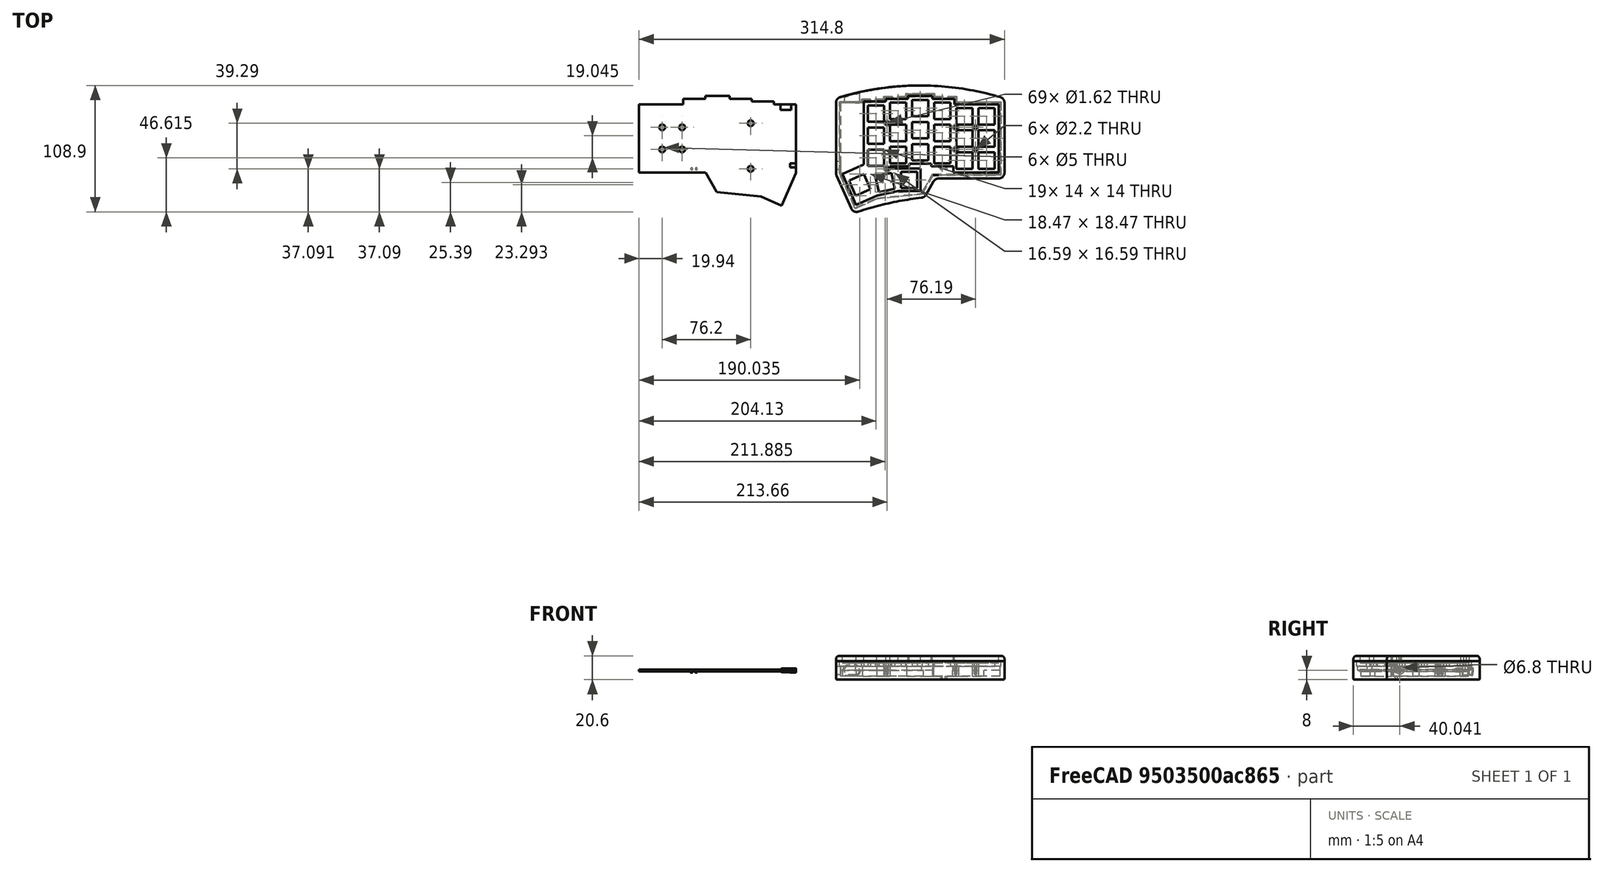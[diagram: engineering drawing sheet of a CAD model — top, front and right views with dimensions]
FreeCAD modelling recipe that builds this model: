
FCSTD DOCUMENT  (FreeCAD 0.21R33771 (Git))
Label: tiltedCaseSplitV1
License: All rights reserved
LicenseURL: http://en.wikipedia.org/wiki/All_rights_reserved
objects: Sketcher::SketchObject×10, PartDesign::Pad×10, PartDesign::SubShapeBinder×9, PartDesign::Pocket×8, PartDesign::Fillet×5, PartDesign::Body×3, Part::Mirroring×2, Mesh::Feature×2, PartDesign::ShapeBinder×1, PartDesign::Hole×1
note: 73 computed .brp shape members not serialized (recipe doc carries the construction recipe); baked Part::Feature solids carry a one-line shape summary decoded from their .brp

FEATURE [Sketcher::SketchObject] Sketch024  label="BodySketch"
  FullyConstrained = true
  MapMode = 5
  Support = -> [XY_Plane004]
  sketch-geometry (18):
    g0: LineSegment StartX=-154.9 StartY=-37.98 StartZ=0 EndX=-116.82 EndY=-37.98 EndZ=0
    g1: LineSegment StartX=-116.82 StartY=-37.98 StartZ=0 EndX=-116.82 EndY=-33.217 EndZ=0
    g2: LineSegment StartX=-116.82 StartY=-33.217 StartZ=0 EndX=-97.77 EndY=-33.217 EndZ=0
    g3: LineSegment StartX=-97.77 StartY=-33.217 StartZ=0 EndX=-97.77 EndY=-30.836 EndZ=0
    g4: LineSegment StartX=-97.77 StartY=-30.836 StartZ=0 EndX=-76.92 EndY=-30.836 EndZ=0
    g5: LineSegment StartX=-76.92 StartY=-30.836 StartZ=0 EndX=-76.92 EndY=-33.217 EndZ=0
    g6: LineSegment StartX=-76.92 StartY=-33.217 StartZ=0 EndX=-57.87 EndY=-33.217 EndZ=0
    g7: LineSegment StartX=-57.87 StartY=-33.217 StartZ=0 EndX=-57.87 EndY=-35.598 EndZ=0
    g8: LineSegment StartX=-57.87 StartY=-35.598 StartZ=0 EndX=-38.82 EndY=-35.598 EndZ=0
    g9: LineSegment StartX=-38.82 StartY=-35.598 StartZ=0 EndX=-38.82 EndY=-37.979 EndZ=0
    g10: LineSegment StartX=-38.82 StartY=-37.979 StartZ=0 EndX=-19.75 EndY=-37.979 EndZ=0
    g11: LineSegment StartX=-19.75 StartY=-37.979 StartZ=0 EndX=-19.75 EndY=-97.199 EndZ=0
    g12: LineSegment StartX=-19.75 StartY=-97.199 StartZ=0 EndX=-32.2083 EndY=-125.339 EndZ=0
    g13: LineSegment StartX=-32.2083 StartY=-125.339 StartZ=0 EndX=-49.87 EndY=-117.52 EndZ=0
    g14: LineSegment StartX=-49.87 StartY=-117.52 StartZ=0 EndX=-87.8774 EndY=-113.545 EndZ=0
    g15: LineSegment StartX=-87.8774 StartY=-113.545 StartZ=0 EndX=-97.37 EndY=-96.93 EndZ=0
    g16: LineSegment StartX=-97.37 StartY=-96.93 StartZ=0 EndX=-154.9 EndY=-96.93 EndZ=0
    g17: LineSegment StartX=-154.9 StartY=-96.93 StartZ=0 EndX=-154.9 EndY=-37.98 EndZ=0
  constraints (54):
    c: Horizontal(g0)
    c: Coincident(g0,g1)
    c: Vertical(g1)
    c: Coincident(g1,g2)
    c: Horizontal(g2)
    c: Coincident(g2,g3)
    c: Vertical(g3)
    c: Coincident(g3,g4)
    c: Horizontal(g4)
    c: Coincident(g4,g5)
    c: Vertical(g5)
    c: Coincident(g5,g6)
    c: Horizontal(g6)
    c: Coincident(g6,g7)
    c: Vertical(g7)
    c: Coincident(g7,g8)
    c: Horizontal(g8)
    c: Coincident(g8,g9)
    c: Vertical(g9)
    c: Coincident(g9,g10)
    c: Horizontal(g10)
    c: Coincident(g10,g11)
    c: Vertical(g11)
    c: Coincident(g11,g12)
    c: Coincident(g12,g13)
    c: Coincident(g13,g14)
    c: Coincident(g14,g15)
    c: Coincident(g15,g16)
    c: Horizontal(g16)
    c: Coincident(g16,g17)
    c: Coincident(g17,g0)
    c: Vertical(g17)
    c: DistanceX(g0,g-1) = 154.9
    c: DistanceY(g0,g-1) = 37.98
    c: DistanceX(g0,g0) = 38.08
    c: DistanceY(g1,g1) = 4.763
    c: DistanceY(g3,g3) = 2.381
    c: DistanceY(g5,g5) = 2.381
    c: DistanceY(g7,g7) = 2.381
    c: DistanceY(g9,g9) = 2.381
    c: DistanceX(g2,g2) = 19.05
    c: DistanceX(g4,g4) = 20.85
    c: DistanceX(g6,g6) = 19.05
    c: DistanceX(g8,g8) = 19.05
    c: DistanceX(g10,g10) = 19.07
    c: DistanceY(g17,g17) = 58.95
    c: DistanceX(g16,g16) = 57.53
    c: DistanceX(g15,g13) = 47.5
    c: DistanceY(g13,g15) = 20.59
    c: DistanceY(g11,g11) = 59.22
    c: Angle(g11,g12) = 2.72481
    c: Angle(g12,g13) = 1.5708
    c: Angle(g14,g13) = 2.829
    c: Angle(g14,g15) = 2.19405
FEATURE [PartDesign::Pad] Pad010  label="BodyPad"
  Direction = (0,0,1)
  Length = 1.6
  Length2 = 10
  Profile = -> Sketch024
  ReferenceAxis = -> Sketch024 [N_Axis]
  Type = 0
FEATURE [Sketcher::SketchObject] Sketch025  label="SkrewSketch"
  ExternalGeometry = -> [Pad010]
  FullyConstrained = true
  MapMode = 5
  Support = -> [XY_Plane004]
  sketch-geometry (6):
    g0: Circle CenterX=-134.96 CenterY=-57.929 CenterZ=0 NormalX=0 NormalY=0 NormalZ=1 AngleXU=0 Radius=2.5
    g1: Circle CenterX=-117.815 CenterY=-57.929 CenterZ=0 NormalX=0 NormalY=0 NormalZ=1 AngleXU=0 Radius=2.5
    g2: Circle CenterX=-58.76 CenterY=-54.359 CenterZ=0 NormalX=0 NormalY=0 NormalZ=1 AngleXU=0 Radius=2.5
    g3: Circle CenterX=-58.76 CenterY=-93.649 CenterZ=0 NormalX=0 NormalY=0 NormalZ=1 AngleXU=0 Radius=2.5
    g4: Circle CenterX=-117.815 CenterY=-76.979 CenterZ=0 NormalX=0 NormalY=0 NormalZ=1 AngleXU=0 Radius=2.5
    g5: Circle CenterX=-134.96 CenterY=-76.979 CenterZ=0 NormalX=0 NormalY=0 NormalZ=1 AngleXU=0 Radius=2.5
  constraints (18):
    c: Equal(g5,g0)
    c: Equal(g5,g1)
    c: Equal(g5,g4)
    c: Equal(g5,g2)
    c: Equal(g5,g3)
    c: Diameter(g5) = 5
    c: Horizontal(g0,g1)
    c: Horizontal(g5,g4)
    c: Vertical(g0,g5)
    c: Vertical(g1,g4)
    c: Vertical(g2,g3)
    c: DistanceY(g2,g-3) = 16.38
    c: DistanceX(g2,g-3) = 39.01
    c: DistanceX(g0,g1) = 17.145
    c: DistanceY(g5,g0) = 19.05
    c: DistanceY(g3,g2) = 39.29
    c: DistanceY(g3,g4) = 16.67
    c: DistanceX(g0,g2) = 76.2
FEATURE [PartDesign::Pocket] Pocket028  label="ScrewPocket"
  BaseFeature = -> Pad010
  Direction = (0,0,-1)
  Length = 2
  Length2 = 5
  Profile = -> Sketch025
  ReferenceAxis = -> Sketch025 [N_Axis]
  Reversed = true
  Type = 0
FEATURE [PartDesign::SubShapeBinder] Binder006  label="PcbPlateBinder"
  BindCopyOnChange = 0
  BindMode = 0
  ClaimChildren = false
  Context = -> Body005 [Binder006.]
  Fuse = false
  MakeFace = true
  Offset = 1.9
  OffsetFill = false
  OffsetIntersection = false
  OffsetJoinType = 1
  OffsetOpenResult = false
  PartialLoad = false
  Placement = pos=(0,0,4.6) rot=(0,0,1;0rad)
  Relative = true
  Support = -> [Body004[Pad010.Sketch024.]]
  _Version = 2
FEATURE [PartDesign::Pad] Pad011  label="PlateBodyPad"
  Direction = (0,0,1)
  Length = 8.9
  Length2 = 10
  Placement = pos=(0,0,4.6) rot=(0,0,1;0rad)
  Profile = -> Binder006
  Type = 0
FEATURE [Sketcher::SketchObject] Sketch026  label="PlateSwitchSketch"
  FullyConstrained = true
  MapMode = 5
  Support = -> [XY_Plane005]
  expr: Constraints[126] = .Constraints.switchDistance
  expr: Constraints[127] = .Constraints.switchDistance
  expr: Constraints[128] = .Constraints.switchDistance
  sketch-geometry (112):
    g0: Circle CenterX=-134.95 CenterY=-57.93 CenterZ=0 NormalX=0 NormalY=0 NormalZ=1 AngleXU=0 Radius=1.1
    g1: Circle CenterX=-134.95 CenterY=-76.98 CenterZ=0 NormalX=0 NormalY=0 NormalZ=1 AngleXU=0 Radius=1.1
    g2: Circle CenterX=-58.76 CenterY=-54.36 CenterZ=0 NormalX=0 NormalY=0 NormalZ=1 AngleXU=0 Radius=1.1
    g3: Circle CenterX=-58.76 CenterY=-93.65 CenterZ=0 NormalX=0 NormalY=0 NormalZ=1 AngleXU=0 Radius=1.1
    g4: LineSegment StartX=-151.48 StartY=-41.41 StartZ=0 EndX=-151.48 EndY=-55.41 EndZ=0
    g5: LineSegment StartX=-151.48 StartY=-55.41 StartZ=0 EndX=-137.48 EndY=-55.41 EndZ=0
    g6: LineSegment StartX=-137.48 StartY=-55.41 StartZ=0 EndX=-137.48 EndY=-41.41 EndZ=0
    g7: LineSegment StartX=-137.48 StartY=-41.41 StartZ=0 EndX=-151.48 EndY=-41.41 EndZ=0
    g8: GeomPoint X=-144.48 Y=-48.41 Z=0
    g9: LineSegment StartX=-151.48 StartY=-60.46 StartZ=0 EndX=-151.48 EndY=-74.46 EndZ=0
    g10: LineSegment StartX=-151.48 StartY=-74.46 StartZ=0 EndX=-137.48 EndY=-74.46 EndZ=0
    g11: LineSegment StartX=-137.48 StartY=-74.46 StartZ=0 EndX=-137.48 EndY=-60.46 EndZ=0
    g12: LineSegment StartX=-137.48 StartY=-60.46 StartZ=0 EndX=-151.48 EndY=-60.46 EndZ=0
    g13: GeomPoint X=-144.48 Y=-67.46 Z=0
    g14: LineSegment StartX=-151.48 StartY=-79.51 StartZ=0 EndX=-151.48 EndY=-93.51 EndZ=0
    g15: LineSegment StartX=-151.48 StartY=-93.51 StartZ=0 EndX=-137.48 EndY=-93.51 EndZ=0
    g16: LineSegment StartX=-137.48 StartY=-93.51 StartZ=0 EndX=-137.48 EndY=-79.51 EndZ=0
    g17: LineSegment StartX=-137.48 StartY=-79.51 StartZ=0 EndX=-151.48 EndY=-79.51 EndZ=0
    g18: GeomPoint X=-144.48 Y=-86.51 Z=0
    g19: LineSegment StartX=-132.43 StartY=-41.41 StartZ=0 EndX=-132.43 EndY=-55.41 EndZ=0
    g20: LineSegment StartX=-132.43 StartY=-55.41 StartZ=0 EndX=-118.43 EndY=-55.41 EndZ=0
    g21: LineSegment StartX=-118.43 StartY=-55.41 StartZ=0 EndX=-118.43 EndY=-41.41 EndZ=0
    g22: LineSegment StartX=-118.43 StartY=-41.41 StartZ=0 EndX=-132.43 EndY=-41.41 EndZ=0
    g23: GeomPoint X=-125.43 Y=-48.41 Z=0
    g24: LineSegment StartX=-132.43 StartY=-60.46 StartZ=0 EndX=-132.43 EndY=-74.46 EndZ=0
    g25: LineSegment StartX=-132.43 StartY=-74.46 StartZ=0 EndX=-118.43 EndY=-74.46 EndZ=0
    g26: LineSegment StartX=-118.43 StartY=-74.46 StartZ=0 EndX=-118.43 EndY=-60.46 EndZ=0
    g27: LineSegment StartX=-118.43 StartY=-60.46 StartZ=0 EndX=-132.43 EndY=-60.46 EndZ=0
    g28: GeomPoint X=-125.43 Y=-67.46 Z=0
    g29: LineSegment StartX=-132.43 StartY=-79.51 StartZ=0 EndX=-132.43 EndY=-93.51 EndZ=0
    g30: LineSegment StartX=-132.43 StartY=-93.51 StartZ=0 EndX=-118.43 EndY=-93.51 EndZ=0
    g31: LineSegment StartX=-118.43 StartY=-93.51 StartZ=0 EndX=-118.43 EndY=-79.51 EndZ=0
    g32: LineSegment StartX=-118.43 StartY=-79.51 StartZ=0 EndX=-132.43 EndY=-79.51 EndZ=0
    g33: GeomPoint X=-125.43 Y=-86.51 Z=0
    g34: LineSegment StartX=-113.38 StartY=-36.65 StartZ=0 EndX=-113.38 EndY=-50.65 EndZ=0
    g35: LineSegment StartX=-113.38 StartY=-50.65 StartZ=0 EndX=-99.38 EndY=-50.65 EndZ=0
    g36: LineSegment StartX=-99.38 StartY=-50.65 StartZ=0 EndX=-99.38 EndY=-36.65 EndZ=0
    g37: LineSegment StartX=-99.38 StartY=-36.65 StartZ=0 EndX=-113.38 EndY=-36.65 EndZ=0
    g38: GeomPoint X=-106.38 Y=-43.65 Z=0
    g39: LineSegment StartX=-94.33 StartY=-34.27 StartZ=0 EndX=-94.33 EndY=-48.27 EndZ=0
    g40: LineSegment StartX=-94.33 StartY=-48.27 StartZ=0 EndX=-80.33 EndY=-48.27 EndZ=0
    g41: LineSegment StartX=-80.33 StartY=-48.27 StartZ=0 EndX=-80.33 EndY=-34.27 EndZ=0
    g42: LineSegment StartX=-80.33 StartY=-34.27 StartZ=0 EndX=-94.33 EndY=-34.27 EndZ=0
    g43: GeomPoint X=-87.33 Y=-41.27 Z=0
    g44: LineSegment StartX=-75.28 StartY=-36.65 StartZ=0 EndX=-75.28 EndY=-50.65 EndZ=0
    g45: LineSegment StartX=-75.28 StartY=-50.65 StartZ=0 EndX=-61.28 EndY=-50.65 EndZ=0
    g46: LineSegment StartX=-61.28 StartY=-50.65 StartZ=0 EndX=-61.28 EndY=-36.65 EndZ=0
    g47: LineSegment StartX=-61.28 StartY=-36.65 StartZ=0 EndX=-75.28 EndY=-36.65 EndZ=0
    g48: GeomPoint X=-68.28 Y=-43.65 Z=0
    g49: LineSegment StartX=-56.23 StartY=-39.03 StartZ=0 EndX=-56.23 EndY=-53.03 EndZ=0
    g50: LineSegment StartX=-56.23 StartY=-53.03 StartZ=0 EndX=-42.23 EndY=-53.03 EndZ=0
    g51: LineSegment StartX=-42.23 StartY=-53.03 StartZ=0 EndX=-42.23 EndY=-39.03 EndZ=0
    g52: LineSegment StartX=-42.23 StartY=-39.03 StartZ=0 EndX=-56.23 EndY=-39.03 EndZ=0
    g53: GeomPoint X=-49.23 Y=-46.03 Z=0
    g54: LineSegment StartX=-113.38 StartY=-55.7 StartZ=0 EndX=-113.38 EndY=-69.7 EndZ=0
    g55: LineSegment StartX=-113.38 StartY=-69.7 StartZ=0 EndX=-99.38 EndY=-69.7 EndZ=0
    g56: LineSegment StartX=-99.38 StartY=-69.7 StartZ=0 EndX=-99.38 EndY=-55.7 EndZ=0
    g57: LineSegment StartX=-99.38 StartY=-55.7 StartZ=0 EndX=-113.38 EndY=-55.7 EndZ=0
    g58: GeomPoint X=-106.38 Y=-62.7 Z=0
    g59: LineSegment StartX=-113.38 StartY=-74.745 StartZ=0 EndX=-113.38 EndY=-88.745 EndZ=0
    g60: LineSegment StartX=-113.38 StartY=-88.745 StartZ=0 EndX=-99.38 EndY=-88.745 EndZ=0
    g61: LineSegment StartX=-99.38 StartY=-88.745 StartZ=0 EndX=-99.38 EndY=-74.745 EndZ=0
    g62: LineSegment StartX=-99.38 StartY=-74.745 StartZ=0 EndX=-113.38 EndY=-74.745 EndZ=0
    g63: GeomPoint X=-106.38 Y=-81.745 Z=0
    g64: LineSegment StartX=-94.33 StartY=-53.32 StartZ=0 EndX=-94.33 EndY=-67.32 EndZ=0
    g65: LineSegment StartX=-94.33 StartY=-67.32 StartZ=0 EndX=-80.33 EndY=-67.32 EndZ=0
    g66: LineSegment StartX=-80.33 StartY=-67.32 StartZ=0 EndX=-80.33 EndY=-53.32 EndZ=0
    g67: LineSegment StartX=-80.33 StartY=-53.32 StartZ=0 EndX=-94.33 EndY=-53.32 EndZ=0
    g68: GeomPoint X=-87.33 Y=-60.32 Z=0
    g69: LineSegment StartX=-94.33 StartY=-72.365 StartZ=0 EndX=-94.33 EndY=-86.365 EndZ=0
    g70: LineSegment StartX=-94.33 StartY=-86.365 StartZ=0 EndX=-80.33 EndY=-86.365 EndZ=0
    g71: LineSegment StartX=-80.33 StartY=-86.365 StartZ=0 EndX=-80.33 EndY=-72.365 EndZ=0
    g72: LineSegment StartX=-80.33 StartY=-72.365 StartZ=0 EndX=-94.33 EndY=-72.365 EndZ=0
    g73: GeomPoint X=-87.33 Y=-79.365 Z=0
    g74: LineSegment StartX=-75.28 StartY=-55.7 StartZ=0 EndX=-75.28 EndY=-69.7 EndZ=0
    g75: LineSegment StartX=-75.28 StartY=-69.7 StartZ=0 EndX=-61.28 EndY=-69.7 EndZ=0
    g76: LineSegment StartX=-61.28 StartY=-69.7 StartZ=0 EndX=-61.28 EndY=-55.7 EndZ=0
    g77: LineSegment StartX=-61.28 StartY=-55.7 StartZ=0 EndX=-75.28 EndY=-55.7 EndZ=0
    g78: GeomPoint X=-68.28 Y=-62.7 Z=0
    g79: LineSegment StartX=-75.28 StartY=-74.75 StartZ=0 EndX=-75.28 EndY=-88.75 EndZ=0
    g80: LineSegment StartX=-75.28 StartY=-88.75 StartZ=0 EndX=-61.28 EndY=-88.75 EndZ=0
    g81: LineSegment StartX=-61.28 StartY=-88.75 StartZ=0 EndX=-61.28 EndY=-74.75 EndZ=0
    g82: LineSegment StartX=-61.28 StartY=-74.75 StartZ=0 EndX=-75.28 EndY=-74.75 EndZ=0
    g83: GeomPoint X=-68.28 Y=-81.75 Z=0
    g84: LineSegment StartX=-56.23 StartY=-58.08 StartZ=0 EndX=-56.23 EndY=-72.08 EndZ=0
    g85: LineSegment StartX=-56.23 StartY=-72.08 StartZ=0 EndX=-42.23 EndY=-72.08 EndZ=0
    g86: LineSegment StartX=-42.23 StartY=-72.08 StartZ=0 EndX=-42.23 EndY=-58.08 EndZ=0
    g87: LineSegment StartX=-42.23 StartY=-58.08 StartZ=0 EndX=-56.23 EndY=-58.08 EndZ=0
    g88: GeomPoint X=-49.23 Y=-65.08 Z=0
    g89: LineSegment StartX=-56.23 StartY=-77.125 StartZ=0 EndX=-56.23 EndY=-91.125 EndZ=0
    g90: LineSegment StartX=-56.23 StartY=-91.125 StartZ=0 EndX=-42.23 EndY=-91.125 EndZ=0
    g91: LineSegment StartX=-42.23 StartY=-91.125 StartZ=0 EndX=-42.23 EndY=-77.125 EndZ=0
    g92: LineSegment StartX=-42.23 StartY=-77.125 StartZ=0 EndX=-56.23 EndY=-77.125 EndZ=0
    g93: GeomPoint X=-49.23 Y=-84.125 Z=0
    g94: LineSegment StartX=-84.805 StartY=-96.17 StartZ=0 EndX=-84.805 EndY=-110.17 EndZ=0
    g95: LineSegment StartX=-84.805 StartY=-110.17 StartZ=0 EndX=-70.805 EndY=-110.17 EndZ=0
    g96: LineSegment StartX=-70.805 StartY=-110.17 StartZ=0 EndX=-70.805 EndY=-96.17 EndZ=0
    g97: LineSegment StartX=-70.805 StartY=-96.17 StartZ=0 EndX=-84.805 EndY=-96.17 EndZ=0
    g98: GeomPoint X=-77.805 Y=-103.17 Z=0
    g99: LineSegment StartX=-62.3853 StartY=-97.0536 StartZ=0 EndX=-65.2818 EndY=-110.751 EndZ=0
    g100: LineSegment StartX=-65.2818 StartY=-110.751 StartZ=0 EndX=-51.5847 EndY=-113.647 EndZ=0
    g101: LineSegment StartX=-51.5847 StartY=-113.647 StartZ=0 EndX=-48.6882 EndY=-99.95 EndZ=0
    g102: LineSegment StartX=-48.6882 StartY=-99.95 StartZ=0 EndX=-62.3853 EndY=-97.0536 EndZ=0
    g103: GeomPoint X=-56.985 Y=-105.35 Z=0
    g104: LineSegment StartX=-38.702 StartY=-98.2125 StartZ=0 EndX=-44.3695 EndY=-111.014 EndZ=0
    g105: LineSegment StartX=-44.3695 StartY=-111.014 StartZ=0 EndX=-31.568 EndY=-116.682 EndZ=0
    g106: LineSegment StartX=-31.568 StartY=-116.682 StartZ=0 EndX=-25.9005 EndY=-103.88 EndZ=0
    g107: LineSegment StartX=-25.9005 StartY=-103.88 StartZ=0 EndX=-38.702 EndY=-98.2125 EndZ=0
    g108: GeomPoint X=-35.135 Y=-107.447 Z=0
    g109: GeomPoint X=-77.805 Y=-87.5575 Z=0
    g110: Circle CenterX=-117.85 CenterY=-57.93 CenterZ=0 NormalX=0 NormalY=0 NormalZ=1 AngleXU=0 Radius=1.1
    g111: Circle CenterX=-117.85 CenterY=-76.98 CenterZ=0 NormalX=0 NormalY=0 NormalZ=1 AngleXU=0 Radius=1.1
  constraints (292):
    c: Equal(g0,g1)
    c: Equal(g0,g2)
    c: Equal(g0,g3)
    c: Diameter(g0) = 2.2
    c: Vertical(g1,g0)
    c: DistanceY(g1,g0) = 19.05
    c: Vertical(g2,g3)
    c: DistanceY(g3,g2) = 39.29
    c: Coincident(g4,g5)
    c: Coincident(g5,g6)
    c: Coincident(g6,g7)
    c: Coincident(g7,g4)
    c: Horizontal(g5)
    c: Horizontal(g7)
    c: Vertical(g4)
    c: Vertical(g6)
    c: Symmetric(g5,g4,g8)
    c: DistanceX(g7,g7) = 14
    c: Equal(g7,g6)
    c: Coincident(g9,g10)
    c: Coincident(g10,g11)
    c: Coincident(g11,g12)
    c: Coincident(g12,g9)
    c: Horizontal(g10)
    c: Horizontal(g12)
    c: Vertical(g9)
    c: Vertical(g11)
    c: Symmetric(g10,g9,g13)
    c: Equal(g11,g12)
    c: DistanceX(g12,g12) = 14
    c: Coincident(g14,g15)
    c: Coincident(g15,g16)
    c: Coincident(g16,g17)
    c: Coincident(g17,g14)
    c: Horizontal(g15)
    c: Horizontal(g17)
    c: Vertical(g14)
    c: Vertical(g16)
    c: Symmetric(g15,g14,g18)
    c: Equal(g17,g16)
    c: DistanceX(g17,g17) = 14
    c: Coincident(g19,g20)
    c: Coincident(g20,g21)
    c: Coincident(g21,g22)
    c: Coincident(g22,g19)
    c: Horizontal(g20)
    c: Horizontal(g22)
    c: Vertical(g19)
    c: Vertical(g21)
    c: Symmetric(g20,g19,g23)
    c: Equal(g22,g21)
    c: DistanceX(g22,g22) = 14
    c: Horizontal(g23,g8)
    c: DistanceX(g8,g23) = 19.05  'switchDistance'
    c: Vertical(g18,g13)
    c: Symmetric(g18,g8,g13)
    c: Coincident(g24,g25)
    c: Coincident(g25,g26)
    c: Coincident(g26,g27)
    c: Coincident(g27,g24)
    c: Horizontal(g25)
    c: Horizontal(g27)
    c: Vertical(g24)
    c: Vertical(g26)
    c: Symmetric(g25,g24,g28)
    c: Coincident(g29,g30)
    c: Coincident(g30,g31)
    c: Coincident(g31,g32)
    c: Coincident(g32,g29)
    c: Horizontal(g30)
    c: Horizontal(g32)
    c: Vertical(g29)
    c: Vertical(g31)
    c: Symmetric(g30,g29,g33)
    c: Horizontal(g33,g18)
    c: Vertical(g33,g28)
    c: Vertical(g28,g23)
    c: Equal(g27,g26)
    c: DistanceX(g27,g27) = 14
    c: Equal(g32,g31)
    c: DistanceX(g32,g32) = 14
    c: Horizontal(g28,g13)
    c: Coincident(g34,g35)
    c: Coincident(g35,g36)
    c: Coincident(g36,g37)
    c: Coincident(g37,g34)
    c: Horizontal(g35)
    c: Horizontal(g37)
    c: Vertical(g34)
    c: Vertical(g36)
    c: Symmetric(g35,g34,g38)
    c: Coincident(g39,g40)
    c: Coincident(g40,g41)
    c: Coincident(g41,g42)
    c: Coincident(g42,g39)
    c: Horizontal(g40)
    c: Horizontal(g42)
    c: Vertical(g39)
    c: Vertical(g41)
    c: Symmetric(g40,g39,g43)
    c: Coincident(g44,g45)
    c: Coincident(g45,g46)
    c: Coincident(g46,g47)
    c: Coincident(g47,g44)
    c: Horizontal(g45)
    c: Horizontal(g47)
    c: Vertical(g44)
    c: Vertical(g46)
    c: Symmetric(g45,g44,g48)
    c: Coincident(g49,g50)
    c: Coincident(g50,g51)
    c: Coincident(g51,g52)
    c: Coincident(g52,g49)
    c: Horizontal(g50)
    c: Horizontal(g52)
    c: Vertical(g49)
    c: Vertical(g51)
    c: Symmetric(g50,g49,g53)
    c: Equal(g37,g36)
    c: Equal(g42,g41)
    c: Equal(g47,g46)
    c: Equal(g52,g51)
    c: DistanceX(g37,g37) = 14
    c: DistanceX(g42,g42) = 14
    c: DistanceX(g47,g47) = 14
    c: DistanceX(g52,g52) = 14
    c: DistanceX(g23,g38) = 19.05
    c: DistanceX(g38,g43) = 19.05
    c: DistanceX(g43,g48) = 19.05
    c: DistanceX(g48,g53) = 19.05
    c: Coincident(g54,g55)
    c: Coincident(g55,g56)
    c: Coincident(g56,g57)
    c: Coincident(g57,g54)
    c: Horizontal(g55)
    c: Horizontal(g57)
    c: Vertical(g54)
    c: Vertical(g56)
    c: Symmetric(g55,g54,g58)
    c: Coincident(g59,g60)
    c: Coincident(g60,g61)
    c: Coincident(g61,g62)
    c: Coincident(g62,g59)
    c: Horizontal(g60)
    c: Horizontal(g62)
    c: Vertical(g59)
    c: Vertical(g61)
    c: Symmetric(g60,g59,g63)
    c: Equal(g57,g56)
    c: DistanceX(g57,g57) = 14
    c: Equal(g62,g61)
    c: DistanceX(g62,g62) = 14
    c: Vertical(g63,g58)
    c: Vertical(g58,g38)
    c: DistanceY(g11,g5) = 5.05  'switchDepthDistance'
    c: DistanceY(g56,g35) = 5.05
    c: DistanceY(g61,g55) = 5.045
    c: Coincident(g64,g65)
    c: Coincident(g65,g66)
    c: Coincident(g66,g67)
    c: Coincident(g67,g64)
    c: Horizontal(g65)
    c: Horizontal(g67)
    c: Vertical(g64)
    c: Vertical(g66)
    c: Symmetric(g65,g64,g68)
    c: Coincident(g69,g70)
    c: Coincident(g70,g71)
    c: Coincident(g71,g72)
    c: Coincident(g72,g69)
    c: Horizontal(g70)
    c: Horizontal(g72)
    c: Vertical(g69)
    c: Vertical(g71)
    c: Symmetric(g70,g69,g73)
    c: Vertical(g73,g68)
    c: Vertical(g68,g43)
    c: Equal(g67,g66)
    c: DistanceX(g67,g67) = 14
    c: Equal(g72,g71)
    c: DistanceX(g72,g72) = 14
    c: DistanceY(g66,g40) = 5.05
    c: DistanceY(g71,g65) = 5.045
    c: Coincident(g74,g75)
    c: Coincident(g75,g76)
    c: Coincident(g76,g77)
    c: Coincident(g77,g74)
    c: Horizontal(g75)
    c: Horizontal(g77)
    c: Vertical(g74)
    c: Vertical(g76)
    c: Symmetric(g75,g74,g78)
    c: Coincident(g79,g80)
    c: Coincident(g80,g81)
    c: Coincident(g81,g82)
    c: Coincident(g82,g79)
    c: Horizontal(g80)
    c: Horizontal(g82)
    c: Vertical(g79)
    c: Vertical(g81)
    c: Symmetric(g80,g79,g83)
    c: Coincident(g84,g85)
    c: Coincident(g85,g86)
    c: Coincident(g86,g87)
    c: Coincident(g87,g84)
    c: Horizontal(g85)
    c: Horizontal(g87)
    c: Vertical(g84)
    c: Vertical(g86)
    c: Symmetric(g85,g84,g88)
    c: Coincident(g89,g90)
    c: Coincident(g90,g91)
    c: Coincident(g91,g92)
    c: Coincident(g92,g89)
    c: Horizontal(g90)
    c: Horizontal(g92)
    c: Vertical(g89)
    c: Vertical(g91)
    c: Symmetric(g90,g89,g93)
    c: Vertical(g83,g78)
    c: Vertical(g78,g48)
    c: Equal(g77,g76)
    c: DistanceX(g77,g77) = 14
    c: Equal(g82,g81)
    c: DistanceX(g82,g82) = 14
    c: Equal(g87,g86)
    c: Equal(g91,g92)
    c: DistanceX(g87,g87) = 14
    c: DistanceX(g92,g92) = 14
    c: Vertical(g93,g88)
    c: Vertical(g88,g53) = 5.05
    c: DistanceY(g76,g45) = 5.05
    c: DistanceY(g81,g75) = 5.05
    c: DistanceY(g86,g50) = 5.05
    c: DistanceY(g91,g85) = 5.045
    c: Coincident(g94,g95)
    c: Coincident(g95,g96)
    c: Coincident(g96,g97)
    c: Coincident(g97,g94)
    c: Horizontal(g95)
    c: Horizontal(g97)
    c: Vertical(g94)
    c: Vertical(g96)
    c: Symmetric(g95,g94,g98)
    c: Coincident(g99,g100)
    c: Coincident(g100,g101)
    c: Coincident(g101,g102)
    c: Coincident(g102,g99)
    c: Symmetric(g100,g99,g103)
    c: Coincident(g104,g105)
    c: Coincident(g105,g106)
    c: Coincident(g106,g107)
    c: Coincident(g107,g104)
    c: Symmetric(g105,g104,g108)
    c: Equal(g97,g96)
    c: DistanceX(g97,g97) = 14
    c: Symmetric(g70,g79,g109)
    c: Vertical(g109,g98)
    c: Equal(g102,g101)
    c: Equal(g101,g100)
    c: Equal(g100,g99)
    c: Equal(g107,g106)
    c: Equal(g106,g105)
    c: Equal(g105,g104)
    c: Angle(g102,g101) = 1.5708
    c: Angle(g107,g106) = 1.5708
    c: Angle(g99,g96) = 0.208392
    c: Distance(g104,g106) = 14
    c: Distance(g99,g101) = 14
    c: DistanceX(g4,g-1) = 151.48
    c: DistanceY(g4,g-1) = 41.41
    c: DistanceY(g49,g-1) = 39.03
    c: DistanceY(g46,g-1) = 36.65
    c: DistanceY(g41,g-1) = 34.27
    c: DistanceY(g36,g-1) = 36.65
    c: DistanceY(g96,g-1) = 96.17
    c: DistanceY(g101,g-1) = 99.95
    c: DistanceY(g106,g-1) = 103.88
    c: DistanceX(g103,g108) = 21.85
    c: DistanceX(g98,g103) = 20.82
    c: Angle(g104,g101) = 0.208392
    c: DistanceY(g9,g4) = 5.05
    c: DistanceX(g2,g-1) = 58.76
    c: DistanceX(g0,g-1) = 134.95
    c: DistanceY(g2,g-1) = 54.36
    c: DistanceY(g0,g-1) = 57.93
    c: Vertical(g111,g110)
    c: Equal(g0,g110)
    c: Equal(g110,g111)
    c: Horizontal(g110,g0)
    c: Horizontal(g111,g1)
    c: DistanceX(g0,g110) = 17.1
FEATURE [PartDesign::SubShapeBinder] Binder008  label="PcbOuterBinder"
  BindCopyOnChange = 0
  BindMode = 0
  ClaimChildren = false
  Context = -> Body006 [Binder008.]
  Fuse = false
  MakeFace = true
  Offset = 5
  OffsetFill = false
  OffsetIntersection = false
  OffsetJoinType = 1
  OffsetOpenResult = false
  PartialLoad = false
  Relative = true
  Support = -> [Body004[Pad010.Sketch024.]]
  _Version = 2
FEATURE [Sketcher::SketchObject] Sketch027  label="OuterBodySketch"
  AttachmentOffset = pos=(0,0,-7) rot=(0,0,1;0rad)
  ExternalGeometry = -> [Binder008]
  FullyConstrained = true
  MapMode = 5
  Placement = pos=(0,0,-7) rot=(0,0,1;0rad)
  Support = -> [XY_Plane006]
  sketch-geometry (9):
    g0: LineSegment StartX=-159.9 StartY=-32.98 StartZ=0 EndX=-159.9 EndY=-101.93 EndZ=0
    g1: LineSegment StartX=-159.9 StartY=-101.93 StartZ=0 EndX=-100.272 EndY=-101.93 EndZ=0
    g2: LineSegment StartX=-100.272 StartY=-101.93 StartZ=0 EndX=-90.9471 EndY=-118.252 EndZ=0
    g3: LineSegment StartX=-29.6604 StartY=-131.935 StartZ=0 EndX=-14.75 EndY=-98.2563 EndZ=0
    g4: LineSegment StartX=-14.75 StartY=-98.2563 StartZ=0 EndX=-14.75 EndY=-32.979 EndZ=0
    g5: ArcOfCircle CenterX=-120.398 CenterY=-394.245 CenterZ=0 NormalX=0 NormalY=0 NormalZ=1 AngleXU=0 Radius=277.56 StartAngle=1.23776 EndAngle=1.46449
    g6: ArcOfCircle CenterX=-87.3234 CenterY=-263.74 CenterZ=0 NormalX=0 NormalY=0 NormalZ=1 AngleXU=0 Radius=241.904 StartAngle=1.26609 EndAngle=1.87551
    g7: GeomPoint X=-87.345 Y=-25.836 Z=0
    g8: GeomPoint X=-87.345 Y=-21.836 Z=0
  constraints (19):
    c: Coincident(g0,g-3)
    c: Coincident(g0,g-4)
    c: Coincident(g0,g1)
    c: Coincident(g1,g-5)
    c: Coincident(g1,g2)
    c: Coincident(g2,g-6)
    c: Coincident(g3,g-7)
    c: Coincident(g3,g-8)
    c: Coincident(g3,g4)
    c: Coincident(g4,g-9)
    c: PointOnObject(g8,g6)
    c: Symmetric(g-10,g-10,g7)
    c: Vertical(g8,g7)
    c: DistanceY(g7,g8) = 4
    c: Coincident(g6,g4)
    c: Coincident(g6,g0)
    c: Coincident(g5,g3)
    c: Coincident(g5,g2)
    c: Radius(g5) = 277.56
FEATURE [PartDesign::Pad] Pad012  label="OuterBodyPad"
  Direction = (0,0,1)
  Length = 16
  Length2 = 10
  Profile = -> Sketch027
  ReferenceAxis = -> Sketch027 [N_Axis]
  Type = 0
FEATURE [PartDesign::SubShapeBinder] Binder009  label="PcbInnerBinder"
  BindCopyOnChange = 0
  BindMode = 0
  ClaimChildren = false
  Context = -> Body006 [Binder009.]
  Fuse = false
  MakeFace = true
  Offset = 1.2
  OffsetFill = false
  OffsetIntersection = false
  OffsetJoinType = 1
  OffsetOpenResult = false
  PartialLoad = false
  Placement = pos=(0,0,-4) rot=(0,0,1;0rad)
  Relative = true
  Support = -> [Body004[Pad010.Sketch024.]]
  _Version = 2
FEATURE [PartDesign::Pocket] Pocket031  label="InnerPocket"
  BaseFeature = -> Pad012
  Direction = (0,0,-1)
  Length = 8
  Length2 = 5
  Profile = -> Binder009
  Reversed = true
  Type = 1
FEATURE [PartDesign::SubShapeBinder] Binder010  label="PcbCliffBinder"
  BindCopyOnChange = 0
  BindMode = 0
  ClaimChildren = false
  Context = -> Body006 [Binder010.]
  Fuse = false
  MakeFace = true
  Offset = 2
  OffsetFill = false
  OffsetIntersection = false
  OffsetJoinType = 1
  OffsetOpenResult = false
  PartialLoad = false
  Placement = pos=(0,0,4.6) rot=(0,0,1;0rad)
  Relative = true
  Support = -> [Body004[Pad010.Sketch024.]]
  _Version = 2
FEATURE [PartDesign::Pocket] Pocket032  label="CliffPocket"
  BaseFeature = -> Pocket031
  Direction = (0,0,-1)
  Length = 3.4
  Length2 = 5
  Profile = -> Binder010
  Reversed = true
  Type = 1
FEATURE [PartDesign::ShapeBinder] ShapeBinder  label="PcbSkrewBinder"
  Support = -> [Sketch025]
  TraceSupport = false
FEATURE [Sketcher::SketchObject] Sketch  label="SkrewSupportSketch"
  ExternalGeometry = -> [ShapeBinder,Pocket032]
  FullyConstrained = true
  MapMode = 5
  Placement = pos=(0,0,-4) rot=(0,0,1;0rad)
  Support = -> [Pocket032]
  sketch-geometry (30):
    g0: Circle CenterX=-134.96 CenterY=-57.929 CenterZ=0 NormalX=0 NormalY=0 NormalZ=1 AngleXU=0 Radius=2.6
    g1: Circle CenterX=-134.96 CenterY=-76.979 CenterZ=0 NormalX=0 NormalY=0 NormalZ=1 AngleXU=0 Radius=2.6
    g2: Circle CenterX=-117.815 CenterY=-76.979 CenterZ=0 NormalX=0 NormalY=0 NormalZ=1 AngleXU=0 Radius=2.6
    g3: Circle CenterX=-117.815 CenterY=-57.929 CenterZ=0 NormalX=0 NormalY=0 NormalZ=1 AngleXU=0 Radius=2.6
    g4: Circle CenterX=-58.76 CenterY=-54.359 CenterZ=0 NormalX=0 NormalY=0 NormalZ=1 AngleXU=0 Radius=2.6
    g5: Circle CenterX=-58.76 CenterY=-93.649 CenterZ=0 NormalX=0 NormalY=0 NormalZ=1 AngleXU=0 Radius=2.6
    g6: LineSegment StartX=-156.1 StartY=-98.13 StartZ=0 EndX=-142.1 EndY=-98.13 EndZ=0
    g7: LineSegment StartX=-156.1 StartY=-96.13 StartZ=0 EndX=-156.1 EndY=-98.13 EndZ=0
    g8: LineSegment StartX=-156.1 StartY=-36.78 StartZ=0 EndX=-142.1 EndY=-36.78 EndZ=0
    g9: LineSegment StartX=-156.1 StartY=-38.78 StartZ=0 EndX=-156.1 EndY=-36.78 EndZ=0
    g10: LineSegment StartX=-31.5968 StartY=-126.922 StartZ=0 EndX=-50.1829 EndY=-118.694 EndZ=0
    g11: LineSegment StartX=-18.55 StartY=-97.4528 StartZ=0 EndX=-31.5968 EndY=-126.922 EndZ=0
    g12: LineSegment StartX=-88.6141 StartY=-114.675 StartZ=0 EndX=-90.1023 EndY=-112.07 EndZ=0
    g13: LineSegment StartX=-50.1829 StartY=-118.694 StartZ=0 EndX=-88.6141 EndY=-114.675 EndZ=0
    g14: LineSegment StartX=-156.1 StartY=-38.78 StartZ=0 EndX=-142.1 EndY=-38.78 EndZ=0
    g15: LineSegment StartX=-142.1 StartY=-38.78 StartZ=0 EndX=-142.1 EndY=-36.78 EndZ=0
    g16: LineSegment StartX=-156.1 StartY=-96.13 StartZ=0 EndX=-142.1 EndY=-96.13 EndZ=0
    g17: LineSegment StartX=-142.1 StartY=-96.13 StartZ=0 EndX=-142.1 EndY=-98.13 EndZ=0
    g18: LineSegment StartX=-90.1023 StartY=-112.07 StartZ=0 EndX=-50.1829 EndY=-116.245 EndZ=0
    g19: LineSegment StartX=-98.97 StartY=-29.636 StartZ=0 EndX=-75.72 EndY=-29.636 EndZ=0
    g20: LineSegment StartX=-75.72 StartY=-29.636 StartZ=0 EndX=-75.72 EndY=-31.436 EndZ=0
    g21: LineSegment StartX=-75.72 StartY=-31.436 StartZ=0 EndX=-98.97 EndY=-31.436 EndZ=0
    g22: LineSegment StartX=-98.97 StartY=-31.436 StartZ=0 EndX=-98.97 EndY=-29.636 EndZ=0
    g23: LineSegment StartX=-50.1829 StartY=-116.245 StartZ=0 EndX=-32.3624 EndY=-124.134 EndZ=0
    g24: LineSegment StartX=-32.3624 StartY=-124.134 StartZ=0 EndX=-20.55 EndY=-97.4528 EndZ=0
    g25: LineSegment StartX=-20.55 StartY=-97.4528 StartZ=0 EndX=-18.55 EndY=-97.4528 EndZ=0
    g26: LineSegment StartX=-56.67 StartY=-34.398 StartZ=0 EndX=-37.62 EndY=-34.398 EndZ=0
    g27: LineSegment StartX=-37.62 StartY=-34.398 StartZ=0 EndX=-37.62 EndY=-36.198 EndZ=0
    g28: LineSegment StartX=-37.62 StartY=-36.198 StartZ=0 EndX=-56.67 EndY=-36.198 EndZ=0
    g29: LineSegment StartX=-56.67 StartY=-36.198 StartZ=0 EndX=-56.67 EndY=-34.398 EndZ=0
  constraints (74):
    c: Coincident(g0,g-3)
    c: Coincident(g2,g-5)
    c: Coincident(g3,g-4)
    c: Coincident(g4,g-7)
    c: Coincident(g5,g-8)
    c: Equal(g4,g3)
    c: Equal(g4,g0)
    c: Equal(g4,g1)
    c: Equal(g4,g2)
    c: Equal(g4,g5)
    c: Diameter(g4) = 5.2
    c: Coincident(g-6,g1)
    c: Coincident(g-11,g6)
    c: PointOnObject(g6,g-11)
    c: PointOnObject(g7,g-9)
    c: Coincident(g7,g6)
    c: Coincident(g-10,g8)
    c: PointOnObject(g8,g-10)
    c: PointOnObject(g9,g-9)
    c: Coincident(g9,g8)
    c: Coincident(g11,g10)
    c: Coincident(g-14,g12)
    c: PointOnObject(g12,g-14)
    c: Coincident(g13,g12)
    c: DistanceX(g8,g8) = 14
    c: DistanceY(g9,g9) = 2
    c: DistanceY(g7,g7) = 2
    c: DistanceX(g6,g6) = 14
    c: Coincident(g9,g14)
    c: Horizontal(g14)
    c: Coincident(g14,g15)
    c: Coincident(g15,g8)
    c: Vertical(g15)
    c: Coincident(g7,g16)
    c: Horizontal(g16)
    c: Coincident(g16,g17)
    c: Coincident(g17,g6)
    c: Vertical(g17)
    c: Coincident(g12,g18)
    c: Parallel(g18,g-13)
    c: Coincident(g13,g-13)
    c: Coincident(g10,g13)
    c: Distance(g12) = 3
    c: Coincident(g-15,g19)
    c: Coincident(g19,g-15)
    c: Coincident(g19,g20)
    c: Coincident(g20,g21)
    c: Horizontal(g21)
    c: Coincident(g21,g22)
    c: Coincident(g22,g19)
    c: Vertical(g22)
    c: Vertical(g20)
    c: DistanceY(g22,g22) = 1.8
    c: Coincident(g18,g23)
    c: Coincident(g23,g24)
    c: Coincident(g24,g25)
    c: Coincident(g25,g-16)
    c: Coincident(g11,g25)
    c: Parallel(g23,g10)
    c: Parallel(g11,g24)
    c: Horizontal(g25)
    c: DistanceX(g24,g11) = 2
    c: Coincident(g-16,g10)
    c: Vertical(g10,g18)
    c: Coincident(g-17,g26)
    c: Coincident(g26,g-17)
    c: Coincident(g26,g27)
    c: Coincident(g27,g28)
    c: Horizontal(g28)
    c: Coincident(g28,g29)
    c: Coincident(g29,g26)
    c: Vertical(g29)
    c: DistanceY(g28,g26) = 1.8
    c: Vertical(g27)
FEATURE [PartDesign::Pad] Pad  label="SkrewSupportPad"
  BaseFeature = -> Pocket032
  Direction = (0,0,1)
  Length = 5
  Length2 = 10
  Profile = -> Sketch
  ReferenceAxis = -> Sketch [N_Axis]
  Type = 0
FEATURE [Sketcher::SketchObject] Sketch028  label="PlateConnectorSketch"
  FullyConstrained = false
  MapMode = 5
  Placement = pos=(0,0,-4) rot=(0,0,1;0rad)
  Support = -> [Pad]
  sketch-geometry (6):
    g0: Circle CenterX=-117.85 CenterY=-57.929 CenterZ=0 NormalX=0 NormalY=0 NormalZ=1 AngleXU=0 Radius=2.45
    g1: Circle CenterX=-58.76 CenterY=-54.359 CenterZ=0 NormalX=0 NormalY=0 NormalZ=1 AngleXU=0 Radius=2.45
    g2: Circle CenterX=-134.95 CenterY=-57.929 CenterZ=0 NormalX=0 NormalY=0 NormalZ=1 AngleXU=0 Radius=2.45
    g3: Circle CenterX=-134.95 CenterY=-76.979 CenterZ=0 NormalX=0 NormalY=0 NormalZ=1 AngleXU=0 Radius=2.45
    g4: Circle CenterX=-117.85 CenterY=-76.979 CenterZ=0 NormalX=0 NormalY=0 NormalZ=1 AngleXU=0 Radius=2.45
    g5: Circle CenterX=-58.76 CenterY=-93.649 CenterZ=0 NormalX=0 NormalY=0 NormalZ=1 AngleXU=0 Radius=2.45
  constraints (6):
    c: Equal(g2,g3)
    c: Equal(g2,g4)
    c: Equal(g2,g0)
    c: Equal(g2,g5)
    c: Equal(g2,g1)
    c: Diameter(g2) = 4.9
FEATURE [PartDesign::Pad] Pad013  label="PlateConnectorPad"
  BaseFeature = -> Pad
  Direction = (0,0,1)
  Length = 8.6
  Length2 = 10
  Profile = -> Sketch028
  ReferenceAxis = -> Sketch028 [N_Axis]
  Type = 0
FEATURE [Sketcher::SketchObject] Sketch029  label="MiniJackSketch"
  ExternalGeometry = -> [Pocket028]
  FullyConstrained = true
  MapMode = 5
  Placement = pos=(-19.75,0,0) rot=(0.57735,0.57735,0.57735;2.0944rad)
  Support = -> [Pocket028]
  sketch-geometry (1):
    g0: Circle CenterX=-90.699 CenterY=1 CenterZ=0 NormalX=0 NormalY=0 NormalZ=1 AngleXU=0 Radius=1.8
  constraints (3):
    c: DistanceX(g-3,g0) = 6.5
    c: Diameter(g0) = 3.6
    c: DistanceY(g-1,g0) = 1
FEATURE [PartDesign::Pad] Pad014  label="MiniJackPad"
  BaseFeature = -> Pocket028
  Direction = (1,0,0)
  Length = 5
  Length2 = 10
  Profile = -> Sketch029
  ReferenceAxis = -> Sketch029 [N_Axis]
  Reversed = true
  Type = 0
FEATURE [Sketcher::SketchObject] Sketch030  label="UsbcSketch"
  ExternalGeometry = -> [Pad014]
  FullyConstrained = true
  MapMode = 5
  Placement = pos=(0,-37.979,0) rot=(0,0.707107,0.707107;3.14159rad)
  Support = -> [Pad014]
  sketch-geometry (4):
    g0: ArcOfCircle CenterX=25.42 CenterY=1 CenterZ=0 NormalX=0 NormalY=0 NormalZ=1 AngleXU=0 Radius=1.6 StartAngle=1.5708 EndAngle=4.71239
    g1: ArcOfCircle CenterX=31.42 CenterY=1 CenterZ=0 NormalX=0 NormalY=0 NormalZ=1 AngleXU=0 Radius=1.6 StartAngle=4.71239 EndAngle=7.85398
    g2: LineSegment StartX=25.42 StartY=-0.6 StartZ=0 EndX=31.42 EndY=-0.6 EndZ=0
    g3: LineSegment StartX=31.42 StartY=2.6 StartZ=0 EndX=25.42 EndY=2.6 EndZ=0
  constraints (10):
    c: Tangent(g0,g2) = -1.5708
    c: Tangent(g2,g1) = -1.5708
    c: Tangent(g1,g3) = -1.5708
    c: Tangent(g3,g0) = -1.5708
    c: Horizontal(g2)
    c: DistanceY(g0,g0) = 3.2
    c: Horizontal(g0,g1)
    c: DistanceY(g-3,g1) = 1
    c: DistanceX(g0,g1) = 6
    c: DistanceX(g1,g-3) = 7.4
FEATURE [PartDesign::Pad] Pad015  label="UsbcPad"
  BaseFeature = -> Pad014
  Direction = (0,1,-2e-16)
  Length = 5
  Length2 = 10
  Profile = -> Sketch030
  ReferenceAxis = -> Sketch030 [N_Axis]
  Reversed = true
  Type = 0
FEATURE [Sketcher::SketchObject] Sketch031  label="ResetButtonSketch"
  ExternalGeometry = -> [Pad015]
  FullyConstrained = true
  MapMode = 5
  Placement = pos=(0,0,0) rot=(1,0,0;3.14159rad)
  Support = -> [Pad015]
  sketch-geometry (2):
    g0: Circle CenterX=-105.55 CenterY=93.63 CenterZ=0 NormalX=0 NormalY=0 NormalZ=1 AngleXU=0 Radius=0.85
    g1: Circle CenterX=-109.55 CenterY=93.63 CenterZ=0 NormalX=0 NormalY=0 NormalZ=1 AngleXU=0 Radius=0.85
  constraints (6):
    c: Equal(g1,g0)
    c: Diameter(g1) = 1.7
    c: Horizontal(g1,g0)
    c: DistanceX(g1,g0) = 4
    c: DistanceY(g0,g-3) = 3.3
    c: DistanceX(g-3,g1) = 45.35
FEATURE [PartDesign::Pad] Pad016  label="ResetButtonPad"
  BaseFeature = -> Pad015
  Direction = (0,0,-1)
  Length = 1
  Length2 = 10
  Profile = -> Sketch031
  ReferenceAxis = -> Sketch031 [N_Axis]
  Type = 0
FEATURE [PartDesign::Body] Body004  label="PCB"
  Group = -> [Sketch024,Pad010,Sketch025,Pocket028,Sketch029,Pad014,Sketch030,Pad015,Sketch031,Pad016]
  Origin = -> Origin004
  Tip = -> Pad016
FEATURE [PartDesign::SubShapeBinder] Binder  label="MiniJackBinder"
  BindCopyOnChange = 0
  BindMode = 0
  ClaimChildren = false
  Context = -> Body006 [Binder.]
  Fuse = false
  MakeFace = true
  Offset = 1.6
  OffsetFill = false
  OffsetIntersection = false
  OffsetJoinType = 0
  OffsetOpenResult = false
  PartialLoad = false
  Relative = true
  Support = -> [Body004[Pad014.Sketch029.]]
  _Version = 2
FEATURE [PartDesign::Pocket] Pocket  label="MiniJackPocket"
  BaseFeature = -> Pad013
  Direction = (-1,0,0)
  Length = 5
  Length2 = 5
  Profile = -> Binder
  Reversed = true
  Type = 1
FEATURE [PartDesign::SubShapeBinder] Binder011  label="UsbcBinder"
  BindCopyOnChange = 0
  BindMode = 0
  ClaimChildren = false
  Context = -> Body006 [Binder011.]
  Fuse = false
  MakeFace = true
  Offset = 2
  OffsetFill = false
  OffsetIntersection = false
  OffsetJoinType = 0
  OffsetOpenResult = false
  PartialLoad = false
  Relative = true
  Support = -> [Body004[Pad015.Sketch030.]]
  _Version = 2
FEATURE [PartDesign::Pocket] Pocket033  label="UsbcPocket"
  BaseFeature = -> Pocket
  Direction = (0,-1,0)
  Length = 5
  Length2 = 5
  Profile = -> Binder011
  Reversed = true
  Type = 1
FEATURE [PartDesign::SubShapeBinder] Binder012  label="ResetButtonBinder"
  BindCopyOnChange = 0
  BindMode = 0
  ClaimChildren = false
  Context = -> Body006 [Binder012.]
  Fuse = false
  MakeFace = true
  OffsetFill = false
  OffsetIntersection = false
  OffsetJoinType = 0
  OffsetOpenResult = false
  PartialLoad = false
  Relative = true
  Support = -> [Body004[Pad016.Sketch031.]]
  _Version = 2
FEATURE [PartDesign::Pocket] Pocket034  label="ResetButtonPocket"
  BaseFeature = -> Pocket033
  Direction = (0,0,-1)
  Length = 5
  Length2 = 5
  Profile = -> Binder012
  Type = 1
FEATURE [PartDesign::Hole] Hole  label="PlateThreadPockets"
  BaseFeature = -> Pocket034
  CustomThreadClearance = 0
  Depth = 3.5
  DepthType = 0
  Diameter = 1.619
  DrillForDepth = false
  DrillPoint = 1
  DrillPointAngle = 118
  HoleCutCountersinkAngle = 90
  HoleCutCustomValues = false
  HoleCutDepth = 0
  HoleCutDiameter = 6.1
  HoleCutType = 0
  ModelThread = true
  Profile = -> Pad013 [Face82,Face83,Face84,Face81,Face80,Face79]
  Tapered = false
  TaperedAngle = 90
  ThreadClass = 0
  ThreadDepth = 3.5
  ThreadDepthType = 0
  ThreadDirection = 0
  ThreadFit = 0
  ThreadSize = 6
  ThreadType = 1
  Threaded = true
  UseCustomThreadClearance = false
FEATURE [PartDesign::Fillet] Fillet  label="HoleFillet"
  Base = -> Hole [Edge45,Edge10,Edge9,Edge8,Edge12,Edge11]
  BaseFeature = -> Hole
  Radius = 1
  SupportTransform = false
  UseAllEdges = false
FEATURE [PartDesign::SubShapeBinder] Binder013  label="InternalCutoutPlateBinder"
  BindCopyOnChange = 0
  BindMode = 0
  ClaimChildren = false
  Context = -> Body005 [Binder013.]
  Fuse = false
  MakeFace = true
  Offset = -1
  OffsetFill = false
  OffsetIntersection = false
  OffsetJoinType = 1
  OffsetOpenResult = false
  PartialLoad = false
  Placement = pos=(0,0,7.5) rot=(0,0,1;0rad)
  Relative = true
  Support = -> [Body004[Pad010.Sketch024.]]
  _Version = 2
FEATURE [PartDesign::SubShapeBinder] Binder014  label="OuterBodyBinder"
  BindCopyOnChange = 0
  BindMode = 0
  ClaimChildren = false
  Context = -> Body005 [Binder014.]
  Fuse = false
  MakeFace = true
  OffsetFill = false
  OffsetIntersection = false
  OffsetJoinType = 0
  OffsetOpenResult = false
  PartialLoad = false
  Placement = pos=(0,0,16) rot=(0,0,1;0rad)
  Relative = true
  Support = -> [Body006[Pad012.Sketch027.]]
  _Version = 2
FEATURE [PartDesign::Pad] Pad018  label="OuterPadding"
  BaseFeature = -> Pad011
  Direction = (0,0,1)
  Length = 4.6
  Length2 = 10
  Placement = pos=(0,0,4.6) rot=(0,0,1;0rad)
  Profile = -> Binder014
  Type = 0
FEATURE [PartDesign::Pocket] Pocket030  label="PlateSwitchPocket"
  BaseFeature = -> Pad018
  Direction = (0,0,-1)
  Length = 5
  Length2 = 5
  Midplane = true
  Placement = pos=(0,0,4.6) rot=(0,0,1;0rad)
  Profile = -> Sketch026
  ReferenceAxis = -> Sketch026 [N_Axis]
  Type = 1
FEATURE [PartDesign::Pocket] Pocket035  label="InternalPocket"
  BaseFeature = -> Pocket030
  Direction = (0,0,-1)
  Length = 5
  Length2 = 5
  Placement = pos=(0,0,4.6) rot=(0,0,1;0rad)
  Profile = -> Binder013
  Reversed = true
  Type = 1
FEATURE [Sketcher::SketchObject] Sketch032
  ExternalGeometry = -> [Pocket035]
  FullyConstrained = true
  MapMode = 5
  Placement = pos=(0,0,7.5) rot=(0,0,1;0rad)
  Support = -> [Pocket035]
  sketch-geometry (29):
    g0: LineSegment StartX=-87.505 StartY=-93.47 StartZ=0 EndX=-61.28 EndY=-93.47 EndZ=0
    g1: LineSegment StartX=-115.78 StartY=-96.93 StartZ=0 EndX=-115.78 EndY=-91.445 EndZ=0
    g2: LineSegment StartX=-115.78 StartY=-91.445 StartZ=0 EndX=-96.73 EndY=-91.445 EndZ=0
    g3: LineSegment StartX=-96.73 StartY=-91.445 StartZ=0 EndX=-96.73 EndY=-89.065 EndZ=0
    g4: LineSegment StartX=-96.73 StartY=-89.065 StartZ=0 EndX=-77.68 EndY=-89.065 EndZ=0
    g5: GeomPoint X=-77.68 Y=-91.45 Z=0
    g6: LineSegment StartX=-77.68 StartY=-89.065 StartZ=0 EndX=-77.68 EndY=-91.45 EndZ=0
    g7: LineSegment StartX=-77.68 StartY=-91.45 StartZ=0 EndX=-61.28 EndY=-91.45 EndZ=0
    g8: GeomPoint X=-61.28 Y=-93.47 Z=0
    g9: LineSegment StartX=-61.28 StartY=-93.47 StartZ=0 EndX=-61.28 EndY=-91.45 EndZ=0
    g10: GeomPoint X=-68.285 Y=-112.87 Z=0
    g11: LineSegment StartX=-87.505 StartY=-112.87 StartZ=0 EndX=-87.505 EndY=-93.47 EndZ=0
    g12: LineSegment StartX=-68.285 StartY=-112.87 StartZ=0 EndX=-87.505 EndY=-112.87 EndZ=0
    g13: LineSegment StartX=-31.9347 StartY=-124.721 StartZ=0 EndX=-49.9431 EndY=-116.749 EndZ=0
    g14: LineSegment StartX=-68.285 StartY=-112.87 StartZ=0 EndX=-49.9431 EndY=-116.749 EndZ=0
    g15: LineSegment StartX=-38.82 StartY=-37.979 StartZ=0 EndX=-19.75 EndY=-37.979 EndZ=0
    g16: LineSegment StartX=-19.75 StartY=-37.979 StartZ=0 EndX=-19.75 EndY=-97.199 EndZ=0
    g17: LineSegment StartX=-38.82 StartY=-89.9581 StartZ=0 EndX=-38.82 EndY=-37.979 EndZ=0
    g18: GeomPoint X=-23.231 Y=-105.062 Z=0
    g19: GeomPoint X=-28.8986 Y=-117.863 Z=0
    g20: LineSegment StartX=-31.568 StartY=-116.682 StartZ=0 EndX=-28.8986 EndY=-117.863 EndZ=0
    g21: LineSegment StartX=-25.9005 StartY=-103.88 StartZ=0 EndX=-23.231 EndY=-105.062 EndZ=0
    g22: LineSegment StartX=-19.75 StartY=-97.199 StartZ=0 EndX=-20.1949 EndY=-98.2039 EndZ=0
    g23: LineSegment StartX=-20.1949 StartY=-98.2039 StartZ=0 EndX=-38.82 EndY=-89.9581 EndZ=0
    g24: LineSegment StartX=-115.78 StartY=-96.93 StartZ=0 EndX=-97.37 EndY=-96.93 EndZ=0
    g25: LineSegment StartX=-97.37 StartY=-96.93 StartZ=0 EndX=-87.8774 EndY=-113.545 EndZ=0
    g26: LineSegment StartX=-87.8774 StartY=-113.545 StartZ=0 EndX=-49.87 EndY=-117.52 EndZ=0
    g27: LineSegment StartX=-49.87 StartY=-117.52 StartZ=0 EndX=-32.2083 EndY=-125.339 EndZ=0
    g28: LineSegment StartX=-32.2083 StartY=-125.339 StartZ=0 EndX=-31.9347 EndY=-124.721 EndZ=0
  constraints (70):
    c: Coincident(g11,g0)
    c: Horizontal(g0)
    c: Vertical(g1)
    c: Coincident(g1,g2)
    c: Horizontal(g2)
    c: Coincident(g2,g3)
    c: Vertical(g3)
    c: Coincident(g3,g4)
    c: Horizontal(g4)
    c: Coincident(g6,g4)
    c: Coincident(g6,g5)
    c: Vertical(g6)
    c: Coincident(g7,g6)
    c: Horizontal(g7)
    c: Coincident(g0,g8)
    c: Coincident(g9,g0)
    c: Coincident(g9,g7)
    c: Vertical(g9)
    c: Coincident(g14,g10)
    c: Coincident(g12,g14)
    c: Vertical(g11)
    c: Coincident(g12,g11)
    c: Coincident(g14,g13)
    c: Coincident(g-9,g15)
    c: Coincident(g15,g-10)
    c: Coincident(g15,g16)
    c: Coincident(g16,g-10)
    c: Coincident(g17,g15)
    c: Vertical(g17)
    c: Parallel(g13,g-5)
    c: PointOnObject(g18,g-11)
    c: PointOnObject(g19,g-11)
    c: Coincident(g20,g-5)
    c: Coincident(g20,g19)
    c: Coincident(g21,g-12)
    c: Coincident(g21,g18)
    c: Parallel(g-5,g20)
    c: Parallel(g-12,g21)
    c: Distance(g13,g19) = 7.5
    c: Coincident(g16,g22)
    c: PointOnObject(g22,g-11)
    c: Coincident(g22,g23)
    c: Coincident(g17,g23)
    c: Distance(g22,g18) = 7.5
    c: Parallel(g-12,g23)
    c: DistanceX(g2,g2) = 19.05
    c: DistanceX(g4,g4) = 19.05
    c: DistanceX(g1,g-13) = 2.4
    c: Coincident(g1,g24)
    c: Coincident(g24,g-15)
    c: Horizontal(g24)
    c: Coincident(g24,g25)
    c: Coincident(g25,g-16)
    c: Coincident(g25,g26)
    c: Coincident(g26,g-17)
    c: Coincident(g26,g27)
    c: Coincident(g27,g-17)
    c: Coincident(g27,g28)
    c: Coincident(g28,g13)
    c: DistanceY(g1,g-13) = 2.7
    c: DistanceY(g4,g-18) = 2.7
    c: DistanceY(g6,g-19) = 2.7
    c: DistanceY(g-20,g0) = 2.7
    c: Vertical(g-19,g7)
    c: DistanceX(g0,g-20) = 2.7
    c: DistanceY(g11,g-21) = 2.7
    c: DistanceX(g-21,g12) = 2.52
    c: Parallel(g12,g-21)
    c: Parallel(g14,g-6)
    c: PointOnObject(g13,g-11)
FEATURE [PartDesign::Pad] Pad017
  BaseFeature = -> Pocket035
  Direction = (0,0,1)
  Length = 6.1
  Length2 = 10
  Placement = pos=(0,0,4.6) rot=(0,0,1;0rad)
  Profile = -> Sketch032
  ReferenceAxis = -> Sketch032 [N_Axis]
  Type = 0
FEATURE [PartDesign::Fillet] Fillet001  label="TopSidefillet"
  Base = -> Pad017 [Edge343,Edge339,Edge335,Edge332,Edge333,Edge337,Edge341]
  BaseFeature = -> Pad017
  Placement = pos=(0,0,4.6) rot=(0,0,1;0rad)
  Radius = 5
  SupportTransform = false
  UseAllEdges = false
FEATURE [PartDesign::Fillet] Fillet002  label="Topfillet"
  Base = -> Fillet001 [Edge41,Edge45,Edge49,Edge60,Edge59,Edge57,Edge55,Edge51,Edge47,Edge43,Edge39,Edge35,Edge37,Edge53]
  BaseFeature = -> Fillet001
  Placement = pos=(0,0,4.6) rot=(0,0,1;0rad)
  Radius = 3
  SupportTransform = false
  UseAllEdges = false
FEATURE [PartDesign::Body] Body005  label="SwitchPlate Left"
  Group = -> [Binder006,Pad011,Binder014,Pad018,Sketch026,Pocket030,Binder013,Pocket035,Sketch032,Pad017,Fillet001,Fillet002]
  Origin = -> Origin005
  Tip = -> Fillet002
FEATURE [Part::Mirroring] Part__Mirroring  label="SwitchPlate Right"
  Base = (1.90735e-06,-71.8332,9.09999)
  Normal = (1,0,-1.19209e-07)
  Source = -> Body005
FEATURE [PartDesign::Fillet] Fillet003  label="BottomSideFillet"
  Base = -> Fillet [Edge64,Edge66,Edge65,Edge51,Edge8,Edge5,Edge18]
  BaseFeature = -> Fillet
  Radius = 5
  SupportTransform = false
  UseAllEdges = false
FEATURE [PartDesign::Fillet] Fillet004  label="BottomFillet"
  Base = -> Fillet003 [Edge1,Edge10,Edge9,Edge11,Edge12,Edge14,Edge16,Edge18,Edge20,Edge21,Edge19,Edge17,Edge15,Edge13]
  BaseFeature = -> Fillet003
  Radius = 1
  SupportTransform = false
  UseAllEdges = false
FEATURE [PartDesign::Body] Body006  label="Body Left"
  Group = -> [Binder008,Sketch027,Pad012,Binder009,Pocket031,Binder010,Pocket032,ShapeBinder,Sketch,Pad,Sketch028,Pad013,Binder,Pocket,Binder011,Pocket033,Binder012,Pocket034,Hole,Fillet,Fillet003,Fillet004]
  Origin = -> Origin006
  Tip = -> Fillet004
FEATURE [Part::Mirroring] Part__Mirroring001  label="Body Right"
  Base = (1.78814e-07,-76.8857,0.99999)
  Normal = (1,0,-1.19209e-07)
  Source = -> Body006
FEATURE [Mesh::Feature] Mesh  label="SwitchPlate Left (Meshed)"
FEATURE [Mesh::Feature] Mesh001  label="SwitchPlate Right (Meshed)"
